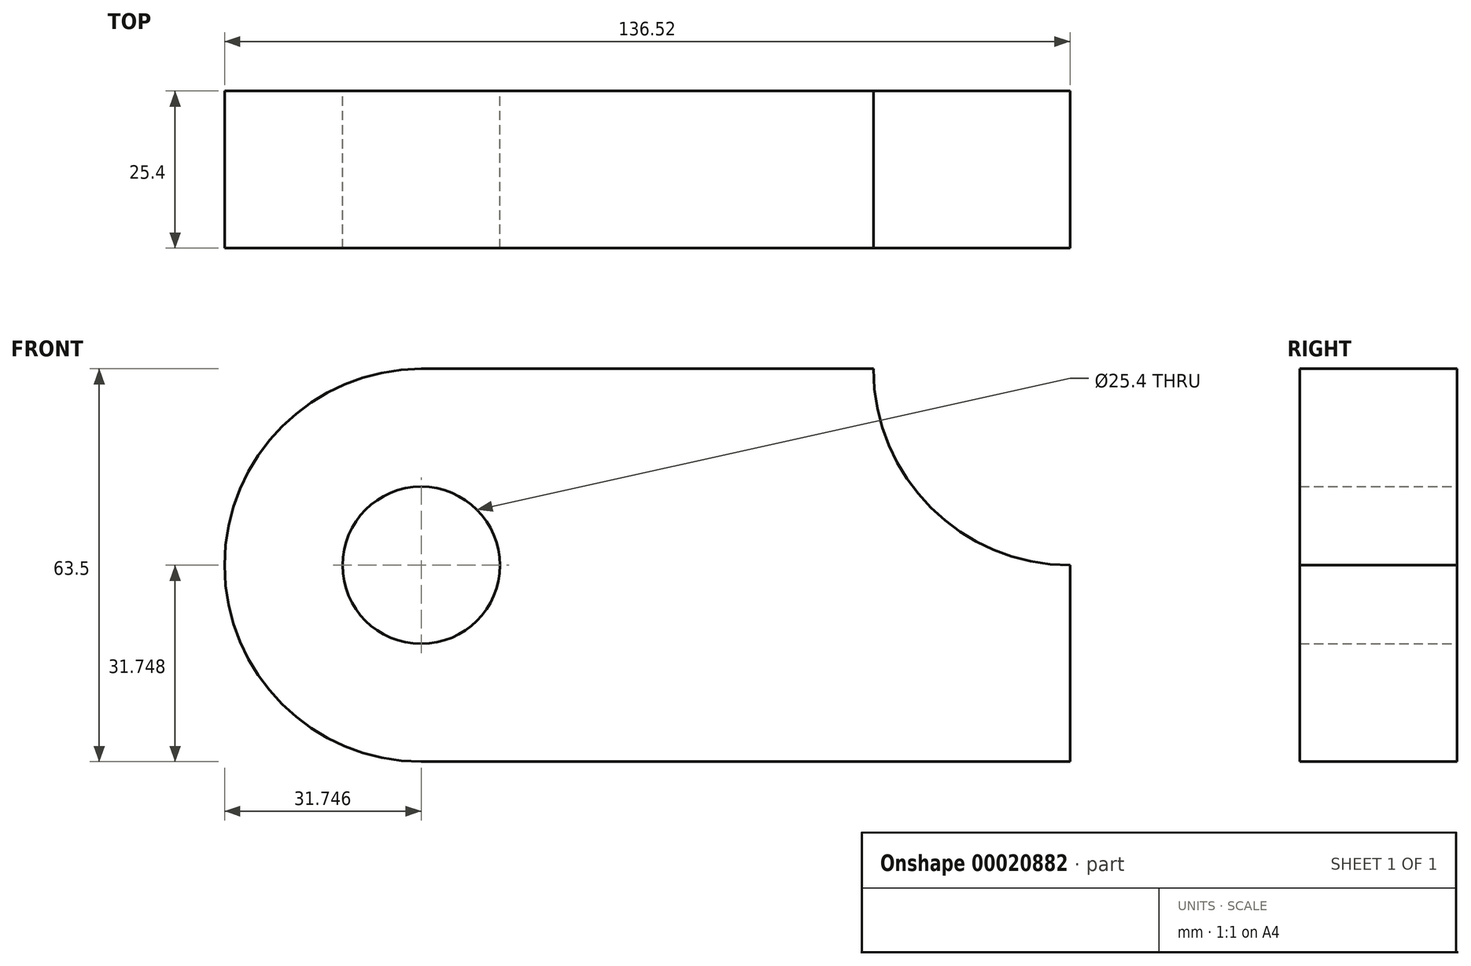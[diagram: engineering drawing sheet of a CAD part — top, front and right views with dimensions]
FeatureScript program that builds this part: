
annotation { "Feature Type Name" : "Feature", "Feature Type Description" : "" }
export const myFeature = defineFeature(function(context is Context, id is Id, definition is map)
    precondition{}
    {
        {
            var Q0;
            Q0=qCreatedBy(makeId("Front.planeOp"),FACE);
            var sketch = newSketch(context, id + "F0", { "sketchPlane" : qUnion([Q0])});
            skLineSegment(sketch, "E0.bottom", {"start": v(-69.04, 19.92) * mm, "end": v(35.73, 19.92) * mm});
            skLineSegment(sketch, "E0.top", {"start": v(-69.04, -43.58) * mm, "end": v(35.73, -43.58) * mm});
            skLineSegment(sketch, "E0.left", {"start": v(-69.04, 19.92) * mm, "end": v(-69.04, -43.58) * mm});
            skLineSegment(sketch, "E0.right", {"start": v(35.73, 19.92) * mm, "end": v(35.73, -43.58) * mm});
            skCircle(sketch, "E1", {"center": v(-69.04, -11.83) * mm, "radius": 31.75 * mm});
            skCircle(sketch, "E2", {"center": v(-69.04, -11.83) * mm, "radius": 12.7 * mm});
            skArc(sketch, "E3", {"start": v(3.98, 19.92) * mm, "mid": v(13.28, -2.53) * mm, "end": v(35.73, -11.83) * mm});
            skSolve(sketch);
        }
        {
            var Q0;
            {var subQ2=sQuery(id+"F0.wireOp",EDGE,"E0.top");Q0=makeQuery(id+"F0.imprint","IMPRINT",FACE,{"disambiguationData":[TD([[makeQuery(id+"F0.imprint","IMPRINT",EDGE,{"derivedFrom":subQ2}),1.0]])]});}
            var Q1;
            {var subQ0=sQuery(id+"F0.wireOp",EDGE,"E2");var subQ1=sQuery(id+"F0.wireOp",EDGE,"E0.left");var subQ3=makeQuery(id+"F0.imprint","INTERSECT",VERTEX,{"disambiguationData":[OD(0.0)],"derivedFrom":[subQ1,subQ0]});Q1=makeQuery(id+"F0.imprint","IMPRINT",FACE,{"disambiguationData":[TD([[makeQuery(id+"F0.imprint","IMPRINT",EDGE,{"disambiguationData":[TD([[subQ3,-1.0]])],"derivedFrom":subQ0}),-1.0]])]});}
            var Q2;
            {var subQ0=sQuery(id+"F0.wireOp",EDGE,"E2");var subQ1=sQuery(id+"F0.wireOp",EDGE,"E0.left");var subQ3=makeQuery(id+"F0.imprint","INTERSECT",VERTEX,{"disambiguationData":[OD(0.0)],"derivedFrom":[subQ1,subQ0]});Q2=makeQuery(id+"F0.imprint","IMPRINT",FACE,{"disambiguationData":[TD([[makeQuery(id+"F0.imprint","IMPRINT",EDGE,{"disambiguationData":[TD([[subQ3,1.0]])],"derivedFrom":subQ0}),-1.0]])]});}
            extrude(context, id + "F1", {"entities" : qUnion([Q0, Q1, Q2]), "depth" : 25.4 * mm});
        }
    });
